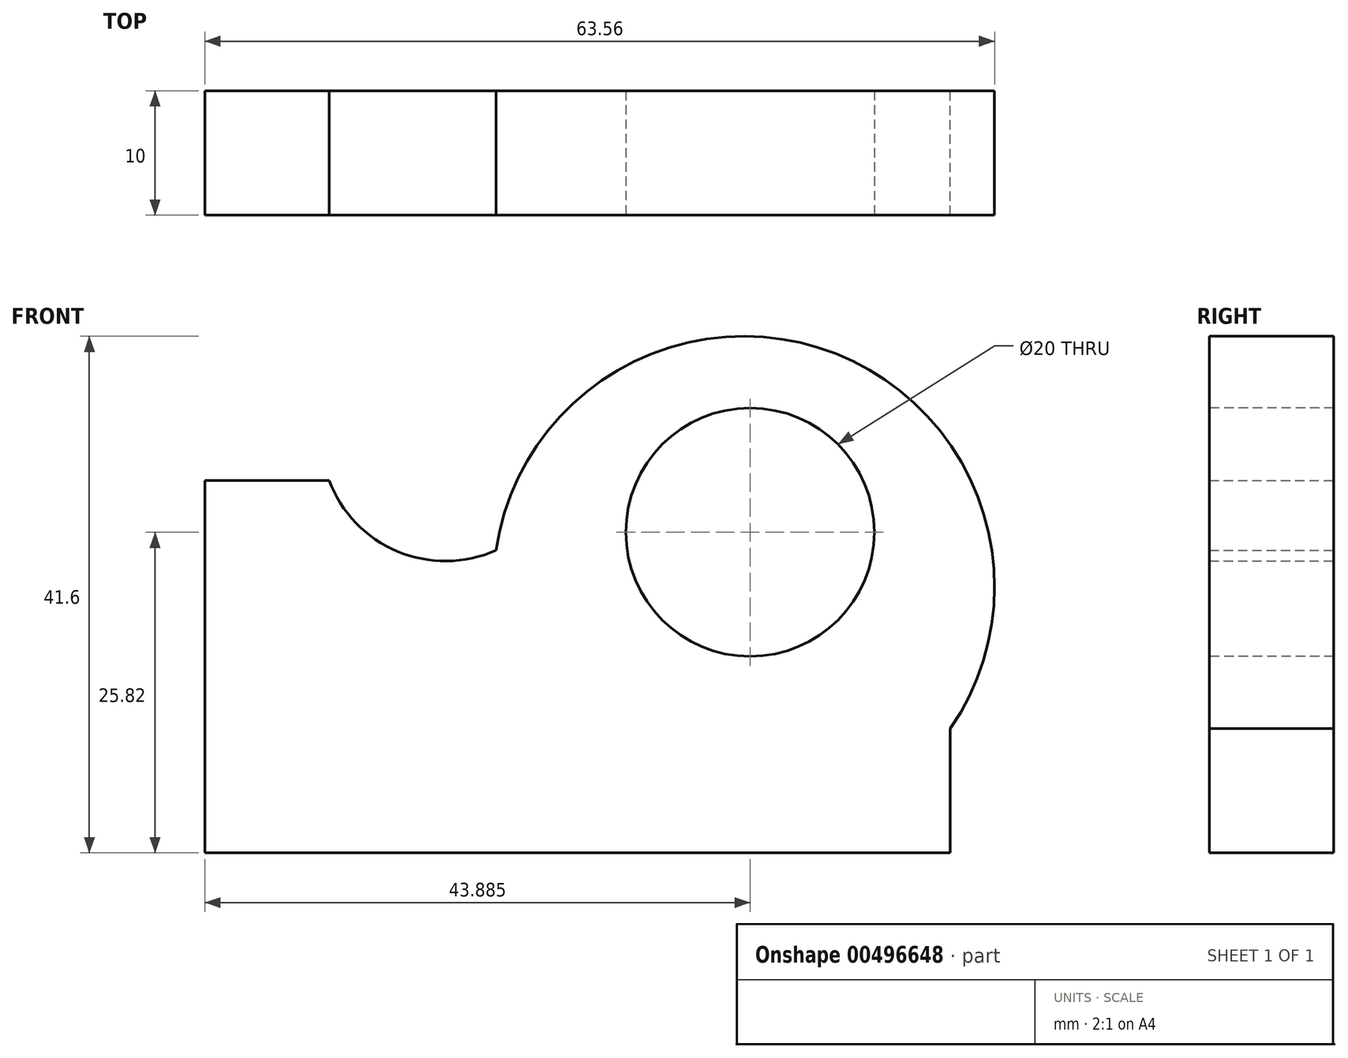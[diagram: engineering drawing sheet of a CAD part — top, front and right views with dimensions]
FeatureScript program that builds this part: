
annotation { "Feature Type Name" : "Feature", "Feature Type Description" : "" }
export const myFeature = defineFeature(function(context is Context, id is Id, definition is map)
    precondition{}
    {
        {
            var Q0;
            Q0=qCreatedBy(makeId("Front.planeOp"),FACE);
            var sketch = newSketch(context, id + "F0", { "sketchPlane" : qUnion([Q0])});
            skLineSegment(sketch, "E0", {"start": v(0, 0) * mm, "end": v(0, 30) * mm});
            skLineSegment(sketch, "E1", {"start": v(0, 0) * mm, "end": v(60, 0) * mm});
            skLineSegment(sketch, "E2", {"start": v(0, 30) * mm, "end": v(10, 30) * mm});
            skLineSegment(sketch, "E3", {"start": v(60, 0) * mm, "end": v(60, 10) * mm});
            skLineSegment(sketch, "E4", {"start": v(60, 10) * mm, "end": v(0, 10) * mm});
            skArc(sketch, "E5", {"start": v(10, 30) * mm, "mid": v(15.5, 24.28) * mm, "end": v(23.44, 24.37) * mm});
            skArc(sketch, "E6.trimOffspring", {"start": v(60, 10) * mm, "mid": v(43.4, 41.6) * mm, "end": v(26.78, 10) * mm});
            skSolve(sketch);
        }
        {
            var Q0;
            {var subQ1=sQuery(id+"F0.wireOp",EDGE,"E1");Q0=makeQuery(id+"F0.imprint","IMPRINT",FACE,{"disambiguationData":[TD([[makeQuery(id+"F0.imprint","IMPRINT",EDGE,{"derivedFrom":subQ1}),1.0]])]});}
            var Q1;
            {var subQ0=sQuery(id+"F0.wireOp",EDGE,"E6.trimOffspring");var subQ4=makeQuery(id+"F0.imprint","INTERSECT",VERTEX,{"derivedFrom":[sQuery(id+"F0.wireOp",EDGE,"E5"),subQ0]});Q1=makeQuery(id+"F0.imprint","IMPRINT",FACE,{"disambiguationData":[TD([[makeQuery(id+"F0.imprint","IMPRINT",EDGE,{"disambiguationData":[TD([[subQ4,-1.0]])],"derivedFrom":subQ0}),1.0]])]});}
            var Q2;
            {var subQ1=sQuery(id+"F0.wireOp",EDGE,"E2");Q2=makeQuery(id+"F0.imprint","IMPRINT",FACE,{"disambiguationData":[TD([[makeQuery(id+"F0.imprint","IMPRINT",EDGE,{"derivedFrom":subQ1}),-1.0]])]});}
            extrude(context, id + "F1", {"entities" : qUnion([Q0, Q1, Q2]), "depth" : 10 * mm, "offsetDistance" : 25 * mm});
        }
        {
            var Q0;
            Q0=makeQuery(id+"F1.opExtrude","CAP_FACE",FACE,{"disambiguationData":[OSD([sQuery(id+"F0.wireOp",EDGE,"E0"),sQuery(id+"F0.wireOp",EDGE,"E1"),sQuery(id+"F0.wireOp",EDGE,"E2"),sQuery(id+"F0.wireOp",EDGE,"E3"),sQuery(id+"F0.wireOp",EDGE,"E5"),sQuery(id+"F0.wireOp",EDGE,"E6.trimOffspring")])],"isStart":false});
            var sketch = newSketch(context, id + "F2", { "sketchPlane" : qUnion([Q0])});
            skCircle(sketch, "E7", {"center": v(43.88, 25.82) * mm, "radius": 10 * mm});
            skSolve(sketch);
        }
        {
            var Q0;
            Q0 = qSketchRegion(id + "F2", true);
            extrude(context, id + "F3", {"entities" : qUnion([Q0]), "operationType" : NewBodyOperationType.REMOVE, "oppositeDirection" : true, "depth" : 10 * mm, "offsetDistance" : 25 * mm});
        }
    });
